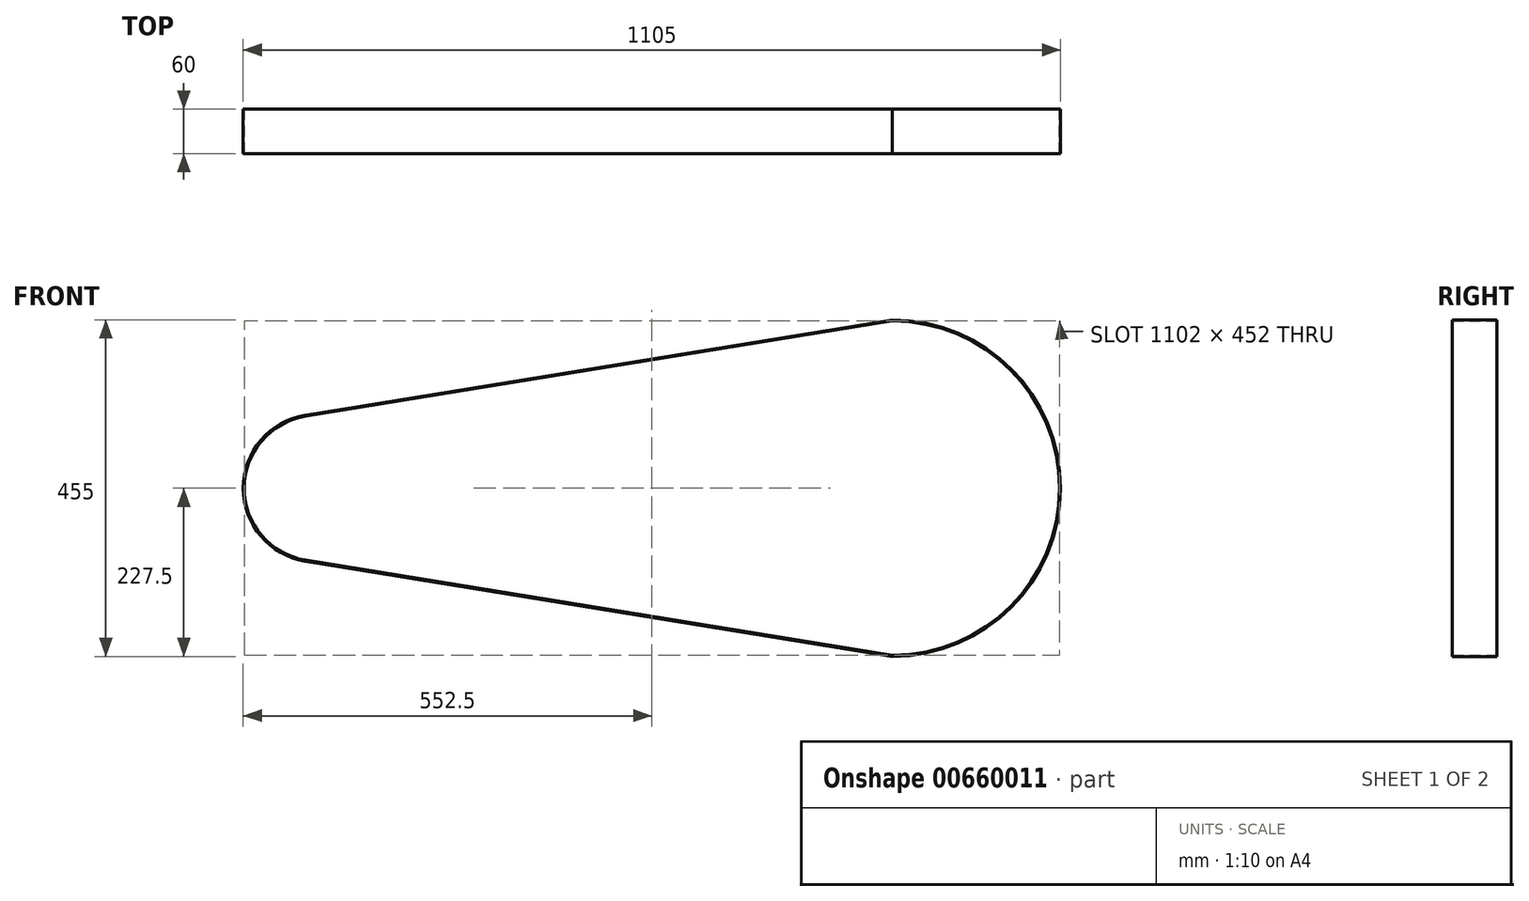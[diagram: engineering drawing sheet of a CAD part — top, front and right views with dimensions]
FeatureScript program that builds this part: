
annotation { "Feature Type Name" : "Feature", "Feature Type Description" : "" }
export const myFeature = defineFeature(function(context is Context, id is Id, definition is map)
    precondition{}
    {
        {
            var Q0;
            Q0=qCreatedBy(makeId("Front.planeOp"),FACE);
            var sketch = newSketch(context, id + "F0", { "sketchPlane" : qUnion([Q0])});
            skLineSegment(sketch, "E0", {"start": v(0, 227.5) * mm, "end": v(-793.52, 98.7) * mm});
            skLineSegment(sketch, "E1", {"start": v(0, -227.5) * mm, "end": v(-793.52, -98.7) * mm});
            skArc(sketch, "E2", {"start": v(0, -227.5) * mm, "mid": v(227.5, 0) * mm, "end": v(0, 227.5) * mm});
            skArc(sketch, "E3", {"start": v(-793.52, 98.7) * mm, "mid": v(-877.5, 0) * mm, "end": v(-793.52, -98.7) * mm});
            skLineSegment(sketch, "E4.0", {"start": v(0.12, 226) * mm, "end": v(-793.28, 97.23) * mm});
            skArc(sketch, "E4.1", {"start": v(0.12, -226) * mm, "mid": v(226, 0) * mm, "end": v(0.12, 226) * mm});
            skLineSegment(sketch, "E4.2", {"start": v(0.12, -226) * mm, "end": v(-793.28, -97.23) * mm});
            skArc(sketch, "E4.3", {"start": v(-793.28, 97.23) * mm, "mid": v(-876, 0) * mm, "end": v(-793.28, -97.23) * mm});
            skSolve(sketch);
        }
        {
            var Q0;
            Q0=makeQuery(id+"F0.imprint","IMPRINT",FACE,{"disambiguationData":[TD([[makeQuery(id+"F0.imprint","IMPRINT",EDGE,{"derivedFrom":sQuery(id+"F0.wireOp",EDGE,"E0")}),1.0]])]});
            extrude(context, id + "F1", {"entities" : qUnion([Q0]), "depth" : 60 * mm, "offsetDistance" : 25 * mm});
        }
    });
